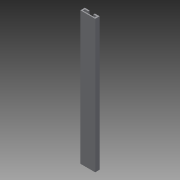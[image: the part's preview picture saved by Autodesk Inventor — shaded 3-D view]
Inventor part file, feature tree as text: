
AUTODESK INVENTOR PART (.ipt)
format: ipt  version: 2014 (Build 180170000, 170)  size: 82,944 bytes
history: native  units: in
note: dims shown in document units (in); Inventor stores cm internally (conversion verified against a paired STEP export)
features: extrude x1, sketch x1
ambient origin geometry x8: Origin, YZ Plane, XZ Plane, XY Plane, X Axis, Y Axis, Z Axis, Center Point
bodies: Solid1 (feature_tree)
feature tree (2):
  extrude  "Extrusion1"  [1 undecoded]
  sketch  "Sketch1"  dims[d0=0.3in d1=0.3225in d2=0.3225in d3=1.0in d4=0.0925in d5=0.0925in d6=0.225in d7=0.225in d8=0.135in d9=9.0in d10=0.0in]
note: 1 required parameter value undecoded (feature->parameter linkage not recoverable at this tier; creation-order binding heuristic only, values carry confidence <= 0.55)
